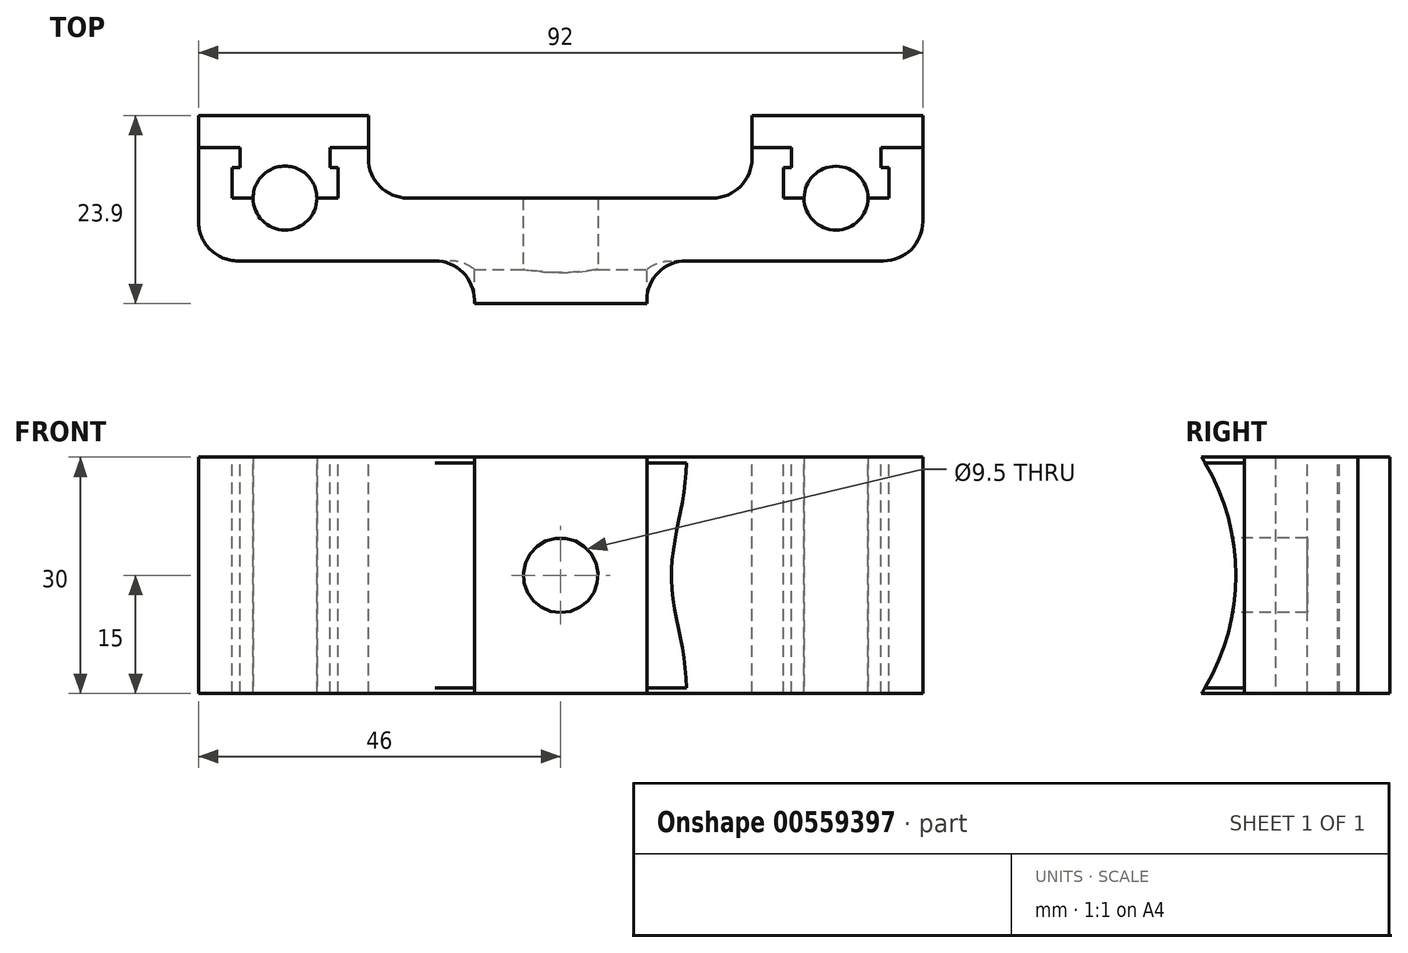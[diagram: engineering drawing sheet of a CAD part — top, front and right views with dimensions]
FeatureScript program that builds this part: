
annotation { "Feature Type Name" : "Feature", "Feature Type Description" : "" }
export const myFeature = defineFeature(function(context is Context, id is Id, definition is map)
    precondition{}
    {
        {
            var Q0;
            Q0=qCreatedBy(makeId("Top.planeOp"),FACE);
            var sketch = newSketch(context, id + "F0", { "sketchPlane" : qUnion([Q0])});
            skLineSegment(sketch, "E0", {"start": v(-46, -4.67) * mm, "end": v(-10.96, -4.67) * mm});
            skLineSegment(sketch, "E1", {"start": v(46, -4.67) * mm, "end": v(46, 9.75) * mm});
            skLineSegment(sketch, "E2", {"start": v(46, 9.75) * mm, "end": v(40.7, 9.75) * mm});
            skLineSegment(sketch, "E3", {"start": v(40.7, 9.75) * mm, "end": v(40.7, 7.2) * mm});
            skLineSegment(sketch, "E4", {"start": v(40.7, 7.2) * mm, "end": v(41.72, 7.2) * mm});
            skLineSegment(sketch, "E5", {"start": v(41.72, 7.2) * mm, "end": v(41.72, 3.31) * mm});
            skLineSegment(sketch, "E6", {"start": v(41.72, 3.31) * mm, "end": v(39.02, 3.31) * mm});
            skLineSegment(sketch, "E7", {"start": v(30.95, 3.31) * mm, "end": v(28.3, 3.31) * mm});
            skLineSegment(sketch, "E8", {"start": v(28.3, 3.31) * mm, "end": v(28.3, 7.2) * mm});
            skLineSegment(sketch, "E9", {"start": v(28.3, 7.2) * mm, "end": v(29.3, 7.2) * mm});
            skLineSegment(sketch, "E10", {"start": v(29.3, 7.2) * mm, "end": v(29.3, 9.74) * mm});
            skLineSegment(sketch, "E11", {"start": v(29.3, 9.74) * mm, "end": v(24.3, 9.75) * mm});
            skLineSegment(sketch, "E12", {"start": v(24.3, 9.75) * mm, "end": v(24.3, 3.31) * mm});
            skLineSegment(sketch, "E13", {"start": v(24.3, 3.31) * mm, "end": v(-24.41, 3.31) * mm});
            skLineSegment(sketch, "E14", {"start": v(-24.41, 3.31) * mm, "end": v(-24.41, 9.74) * mm});
            skLineSegment(sketch, "E15", {"start": v(-24.41, 9.74) * mm, "end": v(-29.3, 9.74) * mm});
            skLineSegment(sketch, "E16", {"start": v(-29.3, 9.74) * mm, "end": v(-29.3, 7.2) * mm});
            skLineSegment(sketch, "E17", {"start": v(-29.3, 7.2) * mm, "end": v(-28.3, 7.2) * mm});
            skLineSegment(sketch, "E18", {"start": v(-28.3, 7.2) * mm, "end": v(-28.3, 3.31) * mm});
            skLineSegment(sketch, "E19", {"start": v(-28.3, 3.31) * mm, "end": v(-30.99, 3.31) * mm});
            skLineSegment(sketch, "E20", {"start": v(-39.04, 3.31) * mm, "end": v(-41.7, 3.31) * mm});
            skLineSegment(sketch, "E21", {"start": v(-41.7, 3.31) * mm, "end": v(-41.7, 7.2) * mm});
            skLineSegment(sketch, "E22", {"start": v(-41.7, 7.2) * mm, "end": v(-40.7, 7.2) * mm});
            skLineSegment(sketch, "E23", {"start": v(-40.7, 7.2) * mm, "end": v(-40.7, 9.74) * mm});
            skLineSegment(sketch, "E24", {"start": v(-40.7, 9.74) * mm, "end": v(-46, 9.74) * mm});
            skLineSegment(sketch, "E25", {"start": v(-46, 9.74) * mm, "end": v(-46, -4.67) * mm});
            skArc(sketch, "E26", {"start": v(-39.08, 3.31) * mm, "mid": v(-35.01, -0.75) * mm, "end": v(-30.95, 3.31) * mm});
            skArc(sketch, "E27", {"start": v(30.92, 3.31) * mm, "mid": v(34.98, -0.75) * mm, "end": v(39.05, 3.31) * mm});
            skLineSegment(sketch, "E28.bottom", {"start": v(10.96, -13.65) * mm, "end": v(-10.96, -13.65) * mm});
            skLineSegment(sketch, "E28.left", {"start": v(10.96, -13.65) * mm, "end": v(10.96, -4.67) * mm});
            skLineSegment(sketch, "E28.right", {"start": v(-10.96, -13.65) * mm, "end": v(-10.96, -4.67) * mm});
            skPoint(sketch, "E28.middle", {"position": v(0, -4.67) * mm});
            skPoint(sketch, "E29.orphan", {"position": v(10.96, 4.32) * mm});
            skPoint(sketch, "E30.orphan", {"position": v(-10.96, 4.32) * mm});
            skLineSegment(sketch, "E31.trimOffspring", {"start": v(10.96, -4.67) * mm, "end": v(46, -4.67) * mm});
            skSolve(sketch);
        }
        {
            var Q0;
            Q0 = qSketchRegion(id + "F0", true);
            extrude(context, id + "F1", {"entities" : qUnion([Q0]), "depth" : 15 * mm, "offsetDistance" : 25 * mm, "hasSecondDirection" : true, "secondDirectionOppositeDirection" : true, "secondDirectionDepth" : 15 * mm});
        }
        {
            var Q0;
            Q0=qCreatedBy(makeId("Right.planeOp"),FACE);
            var sketch = newSketch(context, id + "F2", { "sketchPlane" : qUnion([Q0])});
            skCircle(sketch, "E32", {"center": v(-33.75, 0) * mm, "radius": 28 * mm});
            skSolve(sketch);
        }
        {
            var Q0;
            Q0=makeQuery(id+"F2.imprint","IMPRINT",FACE,{"disambiguationData":[TD([[makeQuery(id+"F2.imprint","IMPRINT",EDGE,{"derivedFrom":sQuery(id+"F2.wireOp",EDGE,"E32")}),1.0]])]});
            extrude(context, id + "F3", {"entities" : qUnion([Q0]), "operationType" : NewBodyOperationType.REMOVE, "oppositeDirection" : true, "depth" : 12 * mm, "offsetDistance" : 25 * mm, "hasSecondDirection" : true, "secondDirectionOppositeDirection" : false, "secondDirectionDepth" : 12 * mm});
        }
        {
            var Q0;
            Q0=qCreatedBy(makeId("Front.planeOp"),FACE);
            var sketch = newSketch(context, id + "F4", { "sketchPlane" : qUnion([Q0])});
            skCircle(sketch, "E33", {"center": v(0, 0) * mm, "radius": 4.75 * mm});
            skSolve(sketch);
        }
        {
            var Q0;
            Q0 = qSketchRegion(id + "F4", true);
            extrude(context, id + "F5", {"entities" : qUnion([Q0]), "operationType" : NewBodyOperationType.REMOVE, "oppositeDirection" : true, "depth" : 4.9 * mm, "offsetDistance" : 25 * mm, "hasSecondDirection" : true, "secondDirectionOppositeDirection" : false, "secondDirectionDepth" : 9.9 * mm});
        }
        {
            var Q0;
            Q0=makeQuery(id+"F1.opExtrude","SWEPT_EDGE",EDGE,{"disambiguationData":[OSD([sQuery(id+"F0.wireOp",EDGE,"E1"),sQuery(id+"F0.wireOp",EDGE,"E31.trimOffspring")])]});
            var Q1;
            Q1=makeQuery(id+"F1.opExtrude","SWEPT_EDGE",EDGE,{"disambiguationData":[OSD([sQuery(id+"F0.wireOp",EDGE,"E0"),sQuery(id+"F0.wireOp",EDGE,"E25")])]});
            var Q2;
            Q2=makeQuery(id+"F1.opExtrude","SWEPT_EDGE",EDGE,{"disambiguationData":[OSD([sQuery(id+"F0.wireOp",EDGE,"E13"),sQuery(id+"F0.wireOp",EDGE,"E14")])]});
            var Q3;
            Q3=makeQuery(id+"F1.opExtrude","SWEPT_EDGE",EDGE,{"disambiguationData":[OSD([sQuery(id+"F0.wireOp",EDGE,"E12"),sQuery(id+"F0.wireOp",EDGE,"E13")])]});
            fillet(context, id + "F6", {"entities" : qUnion([Q0, Q1, Q2, Q3]), "radius" : 5 * mm, "tangentPropagation" : true, "allowEdgeOverflow" : false});
        }
        {
            var Q0;
            Q0=makeQuery(id+"F1.opExtrude","SWEPT_EDGE",EDGE,{"disambiguationData":[OSD([sQuery(id+"F0.wireOp",EDGE,"E0"),sQuery(id+"F0.wireOp",EDGE,"E28.right")])]});
            var Q1;
            Q1=makeQuery(id+"F1.opExtrude","SWEPT_EDGE",EDGE,{"disambiguationData":[OSD([sQuery(id+"F0.wireOp",EDGE,"E28.left"),sQuery(id+"F0.wireOp",EDGE,"E31.trimOffspring")])]});
            fillet(context, id + "F7", {"entities" : qUnion([Q0, Q1]), "radius" : 5 * mm, "tangentPropagation" : true, "allowEdgeOverflow" : false});
        }
        {
            var Q0;
            Q0=makeQuery(id+"F1.opExtrude","CAP_FACE",FACE,{"disambiguationData":[OSD([sQuery(id+"F0.wireOp",EDGE,"E0"),sQuery(id+"F0.wireOp",EDGE,"E1"),sQuery(id+"F0.wireOp",EDGE,"E2"),sQuery(id+"F0.wireOp",EDGE,"E3"),sQuery(id+"F0.wireOp",EDGE,"E4"),sQuery(id+"F0.wireOp",EDGE,"E5"),sQuery(id+"F0.wireOp",EDGE,"E6"),sQuery(id+"F0.wireOp",EDGE,"E7"),sQuery(id+"F0.wireOp",EDGE,"E8"),sQuery(id+"F0.wireOp",EDGE,"E9"),sQuery(id+"F0.wireOp",EDGE,"E10"),sQuery(id+"F0.wireOp",EDGE,"E11"),sQuery(id+"F0.wireOp",EDGE,"E12"),sQuery(id+"F0.wireOp",EDGE,"E13"),sQuery(id+"F0.wireOp",EDGE,"E14"),sQuery(id+"F0.wireOp",EDGE,"E15"),sQuery(id+"F0.wireOp",EDGE,"E16"),sQuery(id+"F0.wireOp",EDGE,"E17"),sQuery(id+"F0.wireOp",EDGE,"E18"),sQuery(id+"F0.wireOp",EDGE,"E19"),sQuery(id+"F0.wireOp",EDGE,"E20"),sQuery(id+"F0.wireOp",EDGE,"E21"),sQuery(id+"F0.wireOp",EDGE,"E22"),sQuery(id+"F0.wireOp",EDGE,"E23"),sQuery(id+"F0.wireOp",EDGE,"E24"),sQuery(id+"F0.wireOp",EDGE,"E25"),sQuery(id+"F0.wireOp",EDGE,"E26"),sQuery(id+"F0.wireOp",EDGE,"E27"),sQuery(id+"F0.wireOp",EDGE,"E28.bottom"),sQuery(id+"F0.wireOp",EDGE,"E28.left"),sQuery(id+"F0.wireOp",EDGE,"E28.right"),sQuery(id+"F0.wireOp",EDGE,"E31.trimOffspring")])],"isStart":false});
            var sketch = newSketch(context, id + "F8", { "sketchPlane" : qUnion([Q0])});
            skLineSegment(sketch, "E34", {"start": v(24.3, 9.75) * mm, "end": v(29.3, 9.74) * mm});
            skLineSegment(sketch, "E35", {"start": v(29.3, 9.74) * mm, "end": v(29.3, 7.2) * mm});
            skLineSegment(sketch, "E36", {"start": v(29.3, 7.2) * mm, "end": v(28.3, 7.2) * mm});
            skLineSegment(sketch, "E37", {"start": v(28.3, 7.2) * mm, "end": v(28.3, 3.31) * mm});
            skLineSegment(sketch, "E38", {"start": v(28.3, 3.31) * mm, "end": v(30.92, 3.31) * mm});
            skLineSegment(sketch, "E39", {"start": v(30.92, 3.31) * mm, "end": v(30.94, 3.31) * mm});
            skLineSegment(sketch, "E40", {"start": v(39.05, 3.31) * mm, "end": v(41.72, 3.31) * mm});
            skLineSegment(sketch, "E41", {"start": v(41.72, 3.31) * mm, "end": v(41.72, 7.2) * mm});
            skLineSegment(sketch, "E42", {"start": v(41.72, 7.2) * mm, "end": v(40.7, 7.2) * mm});
            skLineSegment(sketch, "E43", {"start": v(40.7, 7.2) * mm, "end": v(40.7, 9.75) * mm});
            skLineSegment(sketch, "E44", {"start": v(40.7, 9.75) * mm, "end": v(46, 9.75) * mm});
            skLineSegment(sketch, "E45", {"start": v(46, 9.75) * mm, "end": v(46, 13.79) * mm});
            skLineSegment(sketch, "E46", {"start": v(46, 13.79) * mm, "end": v(24.3, 13.79) * mm});
            skLineSegment(sketch, "E47", {"start": v(24.3, 13.79) * mm, "end": v(24.3, 9.75) * mm});
            skArc(sketch, "E48", {"start": v(39.03, 3.31) * mm, "mid": v(34.98, 7.36) * mm, "end": v(30.94, 3.31) * mm});
            skLineSegment(sketch, "E49.trimOffspring", {"start": v(39.03, 3.31) * mm, "end": v(39.05, 3.31) * mm});
            skLineSegment(sketch, "E50", {"start": v(-46, 9.74) * mm, "end": v(-40.7, 9.74) * mm});
            skLineSegment(sketch, "E51", {"start": v(-40.7, 9.74) * mm, "end": v(-40.7, 7.2) * mm});
            skLineSegment(sketch, "E52", {"start": v(-40.7, 7.2) * mm, "end": v(-41.7, 7.2) * mm});
            skLineSegment(sketch, "E53", {"start": v(-41.7, 7.2) * mm, "end": v(-41.7, 3.31) * mm});
            skLineSegment(sketch, "E54", {"start": v(-41.7, 3.31) * mm, "end": v(-39.08, 3.31) * mm});
            skLineSegment(sketch, "E55", {"start": v(-39.08, 3.31) * mm, "end": v(-39.07, 3.31) * mm});
            skLineSegment(sketch, "E56", {"start": v(-30.95, 3.31) * mm, "end": v(-28.3, 3.31) * mm});
            skLineSegment(sketch, "E57", {"start": v(-28.3, 3.31) * mm, "end": v(-28.3, 7.2) * mm});
            skLineSegment(sketch, "E58", {"start": v(-28.3, 7.2) * mm, "end": v(-29.3, 7.2) * mm});
            skLineSegment(sketch, "E59", {"start": v(-29.3, 7.2) * mm, "end": v(-29.3, 9.74) * mm});
            skLineSegment(sketch, "E60", {"start": v(-29.3, 9.74) * mm, "end": v(-24.41, 9.74) * mm});
            skLineSegment(sketch, "E61", {"start": v(-24.41, 9.74) * mm, "end": v(-24.41, 13.79) * mm});
            skLineSegment(sketch, "E62", {"start": v(-24.41, 13.79) * mm, "end": v(-46, 13.79) * mm});
            skLineSegment(sketch, "E63", {"start": v(-46, 13.79) * mm, "end": v(-46, 9.74) * mm});
            skArc(sketch, "E64", {"start": v(-30.96, 3.31) * mm, "mid": v(-35.01, 7.37) * mm, "end": v(-39.07, 3.31) * mm});
            skLineSegment(sketch, "E65.trimOffspring", {"start": v(-30.96, 3.31) * mm, "end": v(-30.95, 3.31) * mm});
            skSolve(sketch);
        }
        {
            var Q0;
            Q0 = qSketchRegion(id + "F8", true);
            extrude(context, id + "F9", {"entities" : qUnion([Q0]), "oppositeDirection" : true, "depth" : 30 * mm, "offsetDistance" : 25 * mm});
        }
    });
